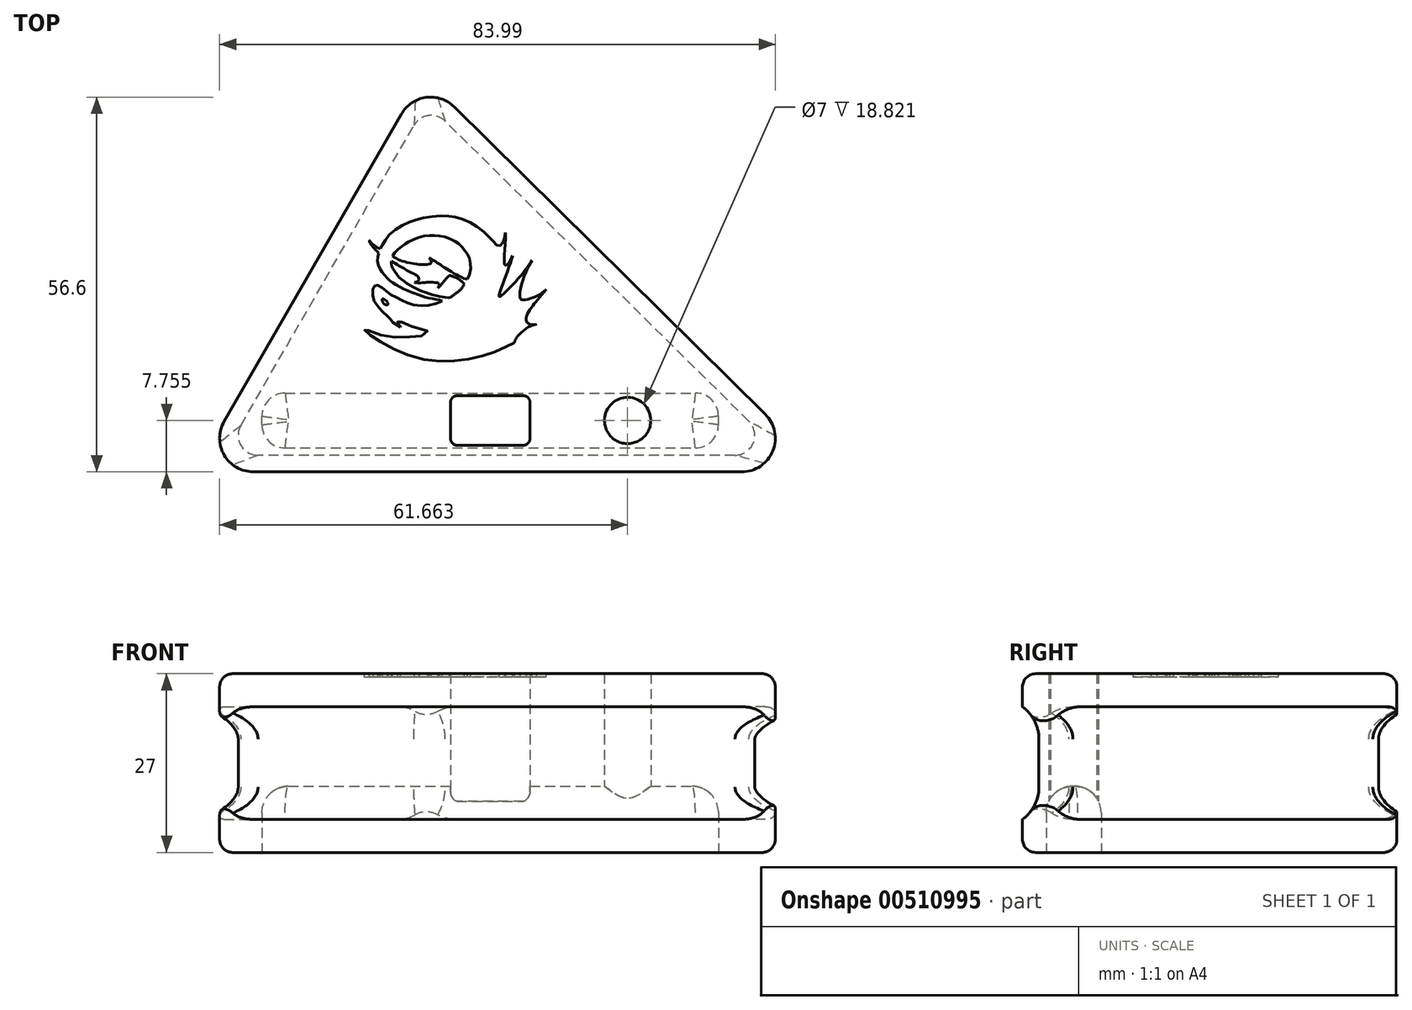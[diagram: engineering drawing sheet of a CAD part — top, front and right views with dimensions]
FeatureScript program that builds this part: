
annotation { "Feature Type Name" : "Feature", "Feature Type Description" : "" }
export const myFeature = defineFeature(function(context is Context, id is Id, definition is map)
    precondition{}
    {
        {
            var Q0;
            Q0=qCreatedBy(makeId("Top.planeOp"),FACE);
            var sketch = newSketch(context, id + "F0", { "sketchPlane" : qUnion([Q0])});
            skLineSegment(sketch, "E0", {"start": v(-34.5, -20.99) * mm, "end": v(60.5, -20.99) * mm});
            skLineSegment(sketch, "E1", {"start": v(0, 38.77) * mm, "end": v(-34.5, -20.99) * mm});
            skLineSegment(sketch, "E2", {"start": v(0, 38.77) * mm, "end": v(60.5, -20.99) * mm});
            skSolve(sketch);
        }
        {
            var Q0;
            Q0=makeQuery(id+"F0.imprint","IMPRINT",FACE,{"disambiguationData":[TD([[makeQuery(id+"F0.imprint","IMPRINT",EDGE,{"derivedFrom":sQuery(id+"F0.wireOp",EDGE,"E0")}),1.0]])]});
            extrude(context, id + "F1", {"entities" : qUnion([Q0]), "depth" : 27 * mm, "offsetDistance" : 25 * mm});
        }
        {
            var Q0;
            Q0=makeQuery(id+"F1.opExtrude","SWEPT_FACE",FACE,{"disambiguationData":[OSD([sQuery(id+"F0.wireOp",EDGE,"E0")])]});
            var sketch = newSketch(context, id + "F2", { "sketchPlane" : qUnion([Q0])});
            skLineSegment(sketch, "E3.bottom", {"start": v(-34.5, 22) * mm, "end": v(60.5, 22) * mm});
            skLineSegment(sketch, "E3.top", {"start": v(-34.5, 5) * mm, "end": v(60.5, 5) * mm});
            skLineSegment(sketch, "E3.left", {"start": v(-34.5, 22) * mm, "end": v(-34.5, 5) * mm});
            skLineSegment(sketch, "E3.right", {"start": v(60.5, 22) * mm, "end": v(60.5, 5) * mm});
            skSolve(sketch);
        }
        {
            var Q0;
            Q0=makeQuery(id+"F2.imprint","IMPRINT",FACE,{"disambiguationData":[TD([[makeQuery(id+"F2.imprint","IMPRINT",EDGE,{"derivedFrom":sQuery(id+"F2.wireOp",EDGE,"E3.bottom")}),-1.0]])]});
            extrude(context, id + "F3", {"entities" : qUnion([Q0]), "operationType" : NewBodyOperationType.REMOVE, "oppositeDirection" : true, "depth" : 2.5 * mm, "offsetDistance" : 25 * mm});
        }
        {
            var Q0;
            Q0=makeQuery(id+"F1.opExtrude","SWEPT_FACE",FACE,{"disambiguationData":[OSD([sQuery(id+"F0.wireOp",EDGE,"E2")])]});
            var sketch = newSketch(context, id + "F4", { "sketchPlane" : qUnion([Q0])});
            skLineSegment(sketch, "E4.bottom", {"start": v(-54.23, 22) * mm, "end": v(27.24, 22) * mm});
            skLineSegment(sketch, "E4.top", {"start": v(-54.23, 5) * mm, "end": v(27.24, 5) * mm});
            skLineSegment(sketch, "E4.left", {"start": v(-54.23, 22) * mm, "end": v(-54.23, 5) * mm});
            skLineSegment(sketch, "E4.right", {"start": v(27.24, 22) * mm, "end": v(27.24, 5) * mm});
            skSolve(sketch);
        }
        {
            var Q0;
            Q0=makeQuery(id+"F4.imprint","IMPRINT",FACE,{"disambiguationData":[TD([[makeQuery(id+"F4.imprint","IMPRINT",EDGE,{"derivedFrom":sQuery(id+"F4.wireOp",EDGE,"E4.bottom")}),-1.0]])]});
            extrude(context, id + "F5", {"entities" : qUnion([Q0]), "operationType" : NewBodyOperationType.REMOVE, "oppositeDirection" : true, "depth" : 2.5 * mm, "offsetDistance" : 25 * mm});
        }
        {
            var Q0;
            Q0=makeQuery(id+"F1.opExtrude","SWEPT_FACE",FACE,{"disambiguationData":[OSD([sQuery(id+"F0.wireOp",EDGE,"E1")])]});
            var sketch = newSketch(context, id + "F6", { "sketchPlane" : qUnion([Q0])});
            skLineSegment(sketch, "E5.bottom", {"start": v(-30.99, 22) * mm, "end": v(32.54, 22) * mm});
            skLineSegment(sketch, "E5.top", {"start": v(-30.99, 5) * mm, "end": v(32.54, 5) * mm});
            skLineSegment(sketch, "E5.left", {"start": v(-30.99, 22) * mm, "end": v(-30.99, 5) * mm});
            skLineSegment(sketch, "E5.right", {"start": v(32.54, 22) * mm, "end": v(32.54, 5) * mm});
            skSolve(sketch);
        }
        {
            var Q0;
            Q0=makeQuery(id+"F6.imprint","IMPRINT",FACE,{"disambiguationData":[TD([[makeQuery(id+"F6.imprint","IMPRINT",EDGE,{"derivedFrom":sQuery(id+"F6.wireOp",EDGE,"E5.bottom")}),-1.0]])]});
            extrude(context, id + "F7", {"entities" : qUnion([Q0]), "operationType" : NewBodyOperationType.REMOVE, "oppositeDirection" : true, "depth" : 2.5 * mm, "offsetDistance" : 25 * mm});
        }
        {
            var Q0;
            Q0=makeQuery(id+"F7.boolean.opBoolean","COPY",EDGE,{"derivedFrom":makeQuery(id+"F7.opExtrude","CAP_EDGE",EDGE,{"disambiguationData":[OSD([sQuery(id+"F6.wireOp",EDGE,"E5.bottom")])],"isStart":false})});
            var Q1;
            Q1=makeQuery(id+"F7.boolean.opBoolean","COPY",EDGE,{"derivedFrom":makeQuery(id+"F7.opExtrude","CAP_EDGE",EDGE,{"disambiguationData":[OSD([sQuery(id+"F6.wireOp",EDGE,"E5.top")])],"isStart":false})});
            var Q2;
            Q2=makeQuery(id+"F3.boolean.opBoolean","COPY",EDGE,{"derivedFrom":makeQuery(id+"F3.opExtrude","CAP_EDGE",EDGE,{"disambiguationData":[OSD([sQuery(id+"F2.wireOp",EDGE,"E3.bottom")])],"isStart":false})});
            var Q3;
            Q3=makeQuery(id+"F3.boolean.opBoolean","COPY",EDGE,{"derivedFrom":makeQuery(id+"F3.opExtrude","CAP_EDGE",EDGE,{"disambiguationData":[OSD([sQuery(id+"F2.wireOp",EDGE,"E3.top")])],"isStart":false})});
            var Q4;
            Q4=makeQuery(id+"F5.boolean.opBoolean","COPY",EDGE,{"derivedFrom":makeQuery(id+"F5.opExtrude","CAP_EDGE",EDGE,{"disambiguationData":[OSD([sQuery(id+"F4.wireOp",EDGE,"E4.bottom")])],"isStart":false})});
            var Q5;
            Q5=makeQuery(id+"F5.boolean.opBoolean","COPY",EDGE,{"derivedFrom":makeQuery(id+"F5.opExtrude","CAP_EDGE",EDGE,{"disambiguationData":[OSD([sQuery(id+"F4.wireOp",EDGE,"E4.top")])],"isStart":false})});
            fillet(context, id + "F8", {"entities" : qUnion([Q0, Q1, Q2, Q3, Q4, Q5]), "radius" : 6 * mm, "tangentPropagation" : true, "allowEdgeOverflow" : false});
        }
        {
            var Q0;
            Q0=makeQuery(id+"F8.opFillet","BLEND_EDGE",EDGE,{"blendedFrom":[makeQuery(id+"F5.boolean.opBoolean","COPY",EDGE,{"derivedFrom":makeQuery(id+"F5.opExtrude","CAP_EDGE",EDGE,{"disambiguationData":[OSD([sQuery(id+"F4.wireOp",EDGE,"E4.bottom")])],"isStart":false})}),makeQuery(id+"F3.boolean.opBoolean","COPY",EDGE,{"derivedFrom":makeQuery(id+"F3.opExtrude","CAP_EDGE",EDGE,{"disambiguationData":[OSD([sQuery(id+"F2.wireOp",EDGE,"E3.bottom")])],"isStart":false})})],"blendedInto":[]});
            var Q1;
            Q1=makeQuery(id+"F8.opFillet","BLEND_EDGE",EDGE,{"blendedFrom":[makeQuery(id+"F7.boolean.opBoolean","COPY",EDGE,{"derivedFrom":makeQuery(id+"F7.opExtrude","CAP_EDGE",EDGE,{"disambiguationData":[OSD([sQuery(id+"F6.wireOp",EDGE,"E5.bottom")])],"isStart":false})}),makeQuery(id+"F5.boolean.opBoolean","COPY",EDGE,{"derivedFrom":makeQuery(id+"F5.opExtrude","CAP_EDGE",EDGE,{"disambiguationData":[OSD([sQuery(id+"F4.wireOp",EDGE,"E4.bottom")])],"isStart":false})})],"blendedInto":[]});
            var Q2;
            Q2=makeQuery(id+"F8.opFillet","BLEND_EDGE",EDGE,{"blendedFrom":[makeQuery(id+"F7.boolean.opBoolean","COPY",EDGE,{"derivedFrom":makeQuery(id+"F7.opExtrude","CAP_EDGE",EDGE,{"disambiguationData":[OSD([sQuery(id+"F6.wireOp",EDGE,"E5.bottom")])],"isStart":false})}),makeQuery(id+"F3.boolean.opBoolean","COPY",EDGE,{"derivedFrom":makeQuery(id+"F3.opExtrude","CAP_EDGE",EDGE,{"disambiguationData":[OSD([sQuery(id+"F2.wireOp",EDGE,"E3.bottom")])],"isStart":false})})],"blendedInto":[]});
            fillet(context, id + "F9", {"entities" : qUnion([Q0, Q1, Q2]), "radius" : 3 * mm, "tangentPropagation" : true, "allowEdgeOverflow" : false});
        }
        {
            var Q0;
            Q0=makeQuery(id+"F1.opExtrude","SWEPT_EDGE",EDGE,{"disambiguationData":[OSD([sQuery(id+"F0.wireOp",EDGE,"F2jWqIrs-Qg5U-4JRb-IFzo-0ohS2Rwvlgda"),sQuery(id+"F0.wireOp",EDGE,"E1")])]});
            var Q1;
            Q1=makeQuery(id+"F1.opExtrude","SWEPT_EDGE",EDGE,{"disambiguationData":[OSD([sQuery(id+"F0.wireOp",EDGE,"E0"),sQuery(id+"F0.wireOp",EDGE,"F2jWqIrs-Qg5U-4JRb-IFzo-0ohS2Rwvlgda")])]});
            var Q2;
            Q2=makeQuery(id+"F1.opExtrude","SWEPT_EDGE",EDGE,{"disambiguationData":[OSD([sQuery(id+"F0.wireOp",EDGE,"E0"),sQuery(id+"F0.wireOp",EDGE,"E1")])]});
            fillet(context, id + "F10", {"entities" : qUnion([Q0, Q1, Q2]), "radius" : 5.08 * mm, "tangentPropagation" : true, "allowEdgeOverflow" : false});
        }
        {
            var Q0;
            Q0=makeQuery(id+"F1.opExtrude","CAP_EDGE",EDGE,{"disambiguationData":[OSD([sQuery(id+"F0.wireOp",EDGE,"E1")])],"isStart":false});
            var Q1;
            Q1=makeQuery(id+"F1.opExtrude","CAP_EDGE",EDGE,{"disambiguationData":[OSD([sQuery(id+"F0.wireOp",EDGE,"E1")])],"isStart":true});
            fillet(context, id + "F11", {"entities" : qUnion([Q0, Q1]), "radius" : 2 * mm, "tangentPropagation" : true, "allowEdgeOverflow" : false});
        }
        {
            var Q0;
            Q0=makeQuery(id+"F0.imprint","IMPRINT",FACE,{"disambiguationData":[TD([[makeQuery(id+"F0.imprint","IMPRINT",EDGE,{"derivedFrom":sQuery(id+"F0.wireOp",EDGE,"E0")}),1.0]])]});
            var sketch = newSketch(context, id + "F12", { "sketchPlane" : qUnion([Q0])});
            skLineSegment(sketch, "E6.bottom", {"start": v(-24.38, -17.39) * mm, "end": v(44.62, -17.39) * mm});
            skLineSegment(sketch, "E6.top", {"start": v(-24.38, -9.09) * mm, "end": v(44.62, -9.09) * mm});
            skLineSegment(sketch, "E6.left", {"start": v(-24.38, -17.39) * mm, "end": v(-24.38, -9.09) * mm});
            skLineSegment(sketch, "E6.right", {"start": v(44.62, -17.39) * mm, "end": v(44.62, -9.09) * mm});
            skSolve(sketch);
        }
        {
            var Q0;
            Q0=makeQuery(id+"F12.imprint","IMPRINT",FACE,{"disambiguationData":[TD([[makeQuery(id+"F12.imprint","IMPRINT",EDGE,{"derivedFrom":sQuery(id+"F12.wireOp",EDGE,"E6.bottom")}),1.0]])]});
            var Q1;
            Q1 = qConstructionFilter(qBodyType(qCreatedBy(id + "F12" ,EDGE), BodyType.WIRE), ConstructionObject.NO);
            extrude(context, id + "F13", {"entities" : qUnion([Q0]), "operationType" : NewBodyOperationType.REMOVE, "surfaceEntities" : qUnion([Q1]), "depth" : 10 * mm, "offsetDistance" : 25 * mm});
        }
        {
            var Q0;
            Q0=makeQuery(id+"F13.boolean.opBoolean","COPY",EDGE,{"derivedFrom":makeQuery(id+"F13.opExtrude","SWEPT_EDGE",EDGE,{"disambiguationData":[OSD([sQuery(id+"F12.wireOp",EDGE,"E6.bottom"),sQuery(id+"F12.wireOp",EDGE,"E6.left")])]})});
            var Q1;
            Q1=makeQuery(id+"F13.boolean.opBoolean","COPY",EDGE,{"derivedFrom":makeQuery(id+"F13.opExtrude","SWEPT_EDGE",EDGE,{"disambiguationData":[OSD([sQuery(id+"F12.wireOp",EDGE,"E6.top"),sQuery(id+"F12.wireOp",EDGE,"E6.left")])]})});
            var Q2;
            Q2=makeQuery(id+"F13.boolean.opBoolean","COPY",EDGE,{"derivedFrom":makeQuery(id+"F13.opExtrude","SWEPT_EDGE",EDGE,{"disambiguationData":[OSD([sQuery(id+"F12.wireOp",EDGE,"E6.bottom"),sQuery(id+"F12.wireOp",EDGE,"E6.right")])]})});
            var Q3;
            Q3=makeQuery(id+"F13.boolean.opBoolean","COPY",EDGE,{"derivedFrom":makeQuery(id+"F13.opExtrude","SWEPT_EDGE",EDGE,{"disambiguationData":[OSD([sQuery(id+"F12.wireOp",EDGE,"E6.top"),sQuery(id+"F12.wireOp",EDGE,"E6.right")])]})});
            fillet(context, id + "F14", {"entities" : qUnion([Q0, Q1, Q2, Q3]), "radius" : 3.5 * mm, "tangentPropagation" : true, "allowEdgeOverflow" : false});
        }
        {
            var Q0;
            Q0=makeQuery(id+"F13.boolean.opBoolean","COPY",EDGE,{"derivedFrom":makeQuery(id+"F13.opExtrude","CAP_EDGE",EDGE,{"disambiguationData":[OSD([sQuery(id+"F12.wireOp",EDGE,"E6.top")])],"isStart":false})});
            var Q1;
            Q1=makeQuery(id+"F13.boolean.opBoolean","COPY",EDGE,{"derivedFrom":makeQuery(id+"F13.opExtrude","CAP_EDGE",EDGE,{"disambiguationData":[OSD([sQuery(id+"F12.wireOp",EDGE,"E6.bottom")])],"isStart":false})});
            fillet(context, id + "F15", {"entities" : qUnion([Q0, Q1]), "radius" : 4 * mm, "tangentPropagation" : true, "allowEdgeOverflow" : false});
        }
        {
            var Q0;
            Q0=makeQuery(id+"F13.boolean.opBoolean","COPY",FACE,{"derivedFrom":makeQuery(id+"F13.opExtrude","CAP_FACE",FACE,{"disambiguationData":[OSD([sQuery(id+"F12.wireOp",EDGE,"E6.bottom"),sQuery(id+"F12.wireOp",EDGE,"E6.top"),sQuery(id+"F12.wireOp",EDGE,"E6.left"),sQuery(id+"F12.wireOp",EDGE,"E6.right")])],"isStart":false})});
            var sketch = newSketch(context, id + "F16", { "sketchPlane" : qUnion([Q0])});
            skLineSegment(sketch, "E7.bottom", {"start": v(16.12, 9.48) * mm, "end": v(4.12, 9.48) * mm});
            skLineSegment(sketch, "E7.top", {"start": v(16.12, 16.98) * mm, "end": v(4.12, 16.98) * mm});
            skLineSegment(sketch, "E7.left", {"start": v(16.12, 9.48) * mm, "end": v(16.12, 16.98) * mm});
            skLineSegment(sketch, "E7.right", {"start": v(4.12, 9.48) * mm, "end": v(4.12, 16.98) * mm});
            skPoint(sketch, "E7.middle", {"position": v(10.12, 13.23) * mm});
            skPoint(sketch, "E7.middle.positionSnap0", {"position": v(10.12, 13.39) * mm});
            skPoint(sketch, "E7.centerSnap0", {"position": v(10.12, 13.39) * mm});
            skSolve(sketch);
        }
        {
            var Q0;
            Q0 = qSketchRegion(id + "F16", true);
            extrude(context, id + "F17", {"entities" : qUnion([Q0]), "operationType" : NewBodyOperationType.REMOVE, "oppositeDirection" : true, "depth" : 19.4 * mm, "hasSecondDirection" : true, "secondDirectionOppositeDirection" : false, "secondDirectionDepth" : 22.6 * mm, "offsetDistance" : 25 * mm});
        }
        {
            var Q0;
            Q0=makeQuery(id+"F17.boolean.opBoolean","COPY",EDGE,{"derivedFrom":makeQuery(id+"F17.opExtrude","SWEPT_EDGE",EDGE,{"disambiguationData":[OSD([sQuery(id+"F16.wireOp",EDGE,"E7.bottom"),sQuery(id+"F16.wireOp",EDGE,"E7.left")])]})});
            var Q1;
            Q1=makeQuery(id+"F17.boolean.opBoolean","COPY",EDGE,{"derivedFrom":makeQuery(id+"F17.opExtrude","SWEPT_EDGE",EDGE,{"disambiguationData":[OSD([sQuery(id+"F16.wireOp",EDGE,"E7.bottom"),sQuery(id+"F16.wireOp",EDGE,"E7.right")])]})});
            var Q2;
            Q2=makeQuery(id+"F17.boolean.opBoolean","COPY",EDGE,{"derivedFrom":makeQuery(id+"F17.opExtrude","SWEPT_EDGE",EDGE,{"disambiguationData":[OSD([sQuery(id+"F16.wireOp",EDGE,"E7.top"),sQuery(id+"F16.wireOp",EDGE,"E7.left")])]})});
            var Q3;
            Q3=makeQuery(id+"F17.boolean.opBoolean","COPY",EDGE,{"derivedFrom":makeQuery(id+"F17.opExtrude","SWEPT_EDGE",EDGE,{"disambiguationData":[OSD([sQuery(id+"F16.wireOp",EDGE,"E7.top"),sQuery(id+"F16.wireOp",EDGE,"E7.right")])]})});
            fillet(context, id + "F18", {"entities" : qUnion([Q0, Q1, Q2, Q3]), "radius" : 1 * mm, "tangentPropagation" : true, "allowEdgeOverflow" : false});
        }
        {
            var Q0;
            Q0=makeQuery(id+"F1.opExtrude","CAP_FACE",FACE,{"disambiguationData":[OSD([sQuery(id+"F0.wireOp",EDGE,"E0"),sQuery(id+"F0.wireOp",EDGE,"E1"),sQuery(id+"F0.wireOp",EDGE,"E2")])],"isStart":false});
            var sketch = newSketch(context, id + "F19", { "sketchPlane" : qUnion([Q0])});
            skFitSpline(sketch, "E8", {"points": [v(2.88, 4.8) * mm, v(1.9, 5.06) * mm, v(0.82, 5.28) * mm, v(-0.36, 5.6) * mm, v(-1.5, 6.03) * mm, v(-3.03, 6.69) * mm, v(-4.46, 7.45) * mm, v(-5.45, 8.26) * mm, v(-6.3, 9.3) * mm, v(-6.88, 10.61) * mm, v(-6.74, 12.05) * mm], "startDerivative": vector(-7.56, 5.16) * mm, "endDerivative": vector(3.22, 10.93) * mm});
            skFitSpline(sketch, "E9", {"points": [v(-6.74, 12.05) * mm, v(-7.2, 12.52) * mm, v(-7.71, 13.12) * mm, v(-8.03, 13.59) * mm, v(-8.16, 13.86) * mm, v(-8.16, 13.93) * mm, v(-7.68, 13.43) * mm, v(-7.17, 13.05) * mm, v(-6.51, 12.73) * mm], "startDerivative": vector(-3.25, 3.3) * mm, "endDerivative": vector(4.22, -0.84) * mm});
            skFitSpline(sketch, "E10", {"points": [v(-6.51, 12.73) * mm, v(-6.35, 12.98) * mm, v(-6.1, 13.43) * mm, v(-5.72, 14.02) * mm, v(-5.16, 14.8) * mm, v(-4.05, 15.7) * mm, v(-2.97, 16.36) * mm, v(-1.85, 16.82) * mm, v(-0.95, 17.12) * mm, v(0.5, 17.43) * mm, v(2.02, 17.64) * mm, v(3.63, 17.64) * mm, v(4.63, 17.52) * mm, v(5.4, 17.32) * mm, v(7, 16.72) * mm, v(8.02, 16.08) * mm, v(9.26, 15.2) * mm, v(10.06, 14.34) * mm, v(10.58, 13.81) * mm, v(11, 13.34) * mm, v(11.25, 13.17) * mm, v(11.49, 13.16) * mm, v(11.78, 13.29) * mm, v(12.02, 13.63) * mm, v(12.24, 14.18) * mm, v(12.36, 14.75) * mm, v(12.4, 15.15) * mm], "startDerivative": vector(6.55, 10.15) * mm, "endDerivative": vector(1.37, 14.38) * mm});
            skFitSpline(sketch, "E11", {"points": [v(12.4, 15.15) * mm, v(12.47, 14.53) * mm, v(12.41, 13.6) * mm, v(12.28, 12.37) * mm, v(12.23, 11.38) * mm, v(12.24, 10.84) * mm, v(12.28, 10.37) * mm, v(12.35, 10.26) * mm, v(12.48, 10.22) * mm, v(12.72, 10.33) * mm, v(13, 10.7) * mm, v(13.5, 11.68) * mm], "startDerivative": vector(1, -6.2) * mm, "endDerivative": vector(3.78, 8.75) * mm});
            skFitSpline(sketch, "E12", {"points": [v(13.5, 11.68) * mm, v(13.25, 10.74) * mm, v(12.86, 9.7) * mm, v(12.4, 8.4) * mm, v(11.98, 7.28) * mm, v(11.63, 6.23) * mm, v(11.46, 5.73) * mm, v(11.43, 5.5) * mm, v(11.46, 5.46) * mm, v(11.6, 5.46) * mm, v(11.9, 5.73) * mm, v(12.4, 6.14) * mm, v(12.95, 6.7) * mm, v(14.02, 7.81) * mm, v(14.96, 8.92) * mm, v(16.47, 10.98) * mm], "startDerivative": vector(-3.06, -14.57) * mm, "endDerivative": vector(13.16, 19.12) * mm});
            skFitSpline(sketch, "E13", {"points": [v(16.47, 10.98) * mm, v(15.36, 8.76) * mm, v(14.76, 6.96) * mm, v(14.58, 5.72) * mm, v(14.62, 5.31) * mm, v(14.79, 5.06) * mm, v(15.1, 4.97) * mm, v(15.62, 5.03) * mm, v(16.4, 5.26) * mm, v(17.19, 5.58) * mm, v(17.97, 6.1) * mm, v(18.58, 6.57) * mm], "startDerivative": vector(-12.66, -21.05) * mm, "endDerivative": vector(6.32, 5.86) * mm});
            skFitSpline(sketch, "E14", {"points": [v(18.58, 6.57) * mm, v(17.02, 4.7) * mm, v(16.3, 3.77) * mm, v(15.64, 2.56) * mm, v(15.57, 1.81) * mm, v(15.78, 1.5) * mm, v(16.09, 1.3) * mm, v(16.61, 1.24) * mm, v(17.13, 1.29) * mm], "startDerivative": vector(-8.12, -9.68) * mm, "endDerivative": vector(5.18, 0.73) * mm});
            skFitSpline(sketch, "E15", {"points": [v(17.13, 1.29) * mm, v(16.1, 0.98) * mm, v(15.32, 0.46) * mm, v(14.71, -0.02) * mm, v(14.36, -0.38) * mm, v(14.02, -0.86) * mm, v(13.8, -1.27) * mm, v(13.77, -1.51) * mm], "startDerivative": vector(-5.77, -1.3) * mm, "endDerivative": vector(-0.14, -2.56) * mm});
            skFitSpline(sketch, "E16", {"points": [v(13.77, -1.51) * mm, v(13.35, -1.69) * mm, v(12.73, -2) * mm, v(12.03, -2.33) * mm, v(10.66, -2.9) * mm, v(9.56, -3.3) * mm, v(8.47, -3.6) * mm, v(6.78, -3.97) * mm, v(5.28, -4.2) * mm, v(3.7, -4.28) * mm, v(2.14, -4.28) * mm, v(0.12, -4.06) * mm, v(-1.93, -3.47) * mm, v(-3.58, -2.81) * mm, v(-5.17, -2.1) * mm, v(-6.55, -1.31) * mm, v(-7.57, -0.63) * mm, v(-8.23, -0.14) * mm, v(-8.56, 0.16) * mm, v(-8.8, 0.38) * mm, v(-8.92, 0.47) * mm, v(-8.92, 0.55) * mm, v(-8.79, 0.6) * mm, v(-8.46, 0.46) * mm, v(-7.53, 0.03) * mm, v(-5.96, -0.47) * mm, v(-4.53, -0.66) * mm, v(-3.13, -0.66) * mm, v(-1.37, -0.57) * mm, v(-0.51, -0.48) * mm, v(0.06, -0.4) * mm, v(0.3, -0.2) * mm, v(0.6, 0.28) * mm, v(0.61, 0.34) * mm, v(0.57, 0.41) * mm, v(0.21, 0.47) * mm, v(-0.46, 0.6) * mm, v(-1.2, 0.77) * mm, v(-2.09, 1.11) * mm, v(-2.9, 1.46) * mm, v(-3.43, 1.7) * mm, v(-3.73, 1.83) * mm, v(-3.87, 1.81) * mm, v(-3.95, 1.69) * mm, v(-3.8, 1.4) * mm, v(-3.52, 1.08) * mm, v(-3.47, 0.97) * mm, v(-3.45, 0.88) * mm], "startDerivative": vector(-23.7, -9.36) * mm, "endDerivative": vector(2.17, -11.37) * mm});
            skFitSpline(sketch, "E17", {"points": [v(-3.45, 0.88) * mm, v(-3.68, 1) * mm, v(-4.26, 1.38) * mm, v(-4.79, 1.79) * mm, v(-5.15, 2.27) * mm, v(-5.62, 2.71) * mm, v(-6.27, 3.35) * mm, v(-6.77, 3.92) * mm, v(-7.08, 4.3) * mm, v(-7.38, 4.72) * mm, v(-7.6, 5.68) * mm, v(-7.59, 6.65) * mm, v(-7.41, 7) * mm, v(-7.17, 7.2) * mm, v(-6.87, 7.18) * mm, v(-6.23, 6.8) * mm, v(-5.56, 6.28) * mm, v(-4.74, 5.67) * mm, v(-3.8, 5.21) * mm, v(-2.79, 4.7) * mm, v(-1.65, 4.3) * mm, v(0, 4.1) * mm, v(1.47, 4.3) * mm, v(2.88, 4.8) * mm], "startDerivative": vector(-8.16, 4.17) * mm, "endDerivative": vector(15.97, 12.28) * mm});
            skFitSpline(sketch, "E18", {"points": [v(6.2, 7.3) * mm, v(5.96, 7.62) * mm, v(5.5, 8.01) * mm, v(4.98, 8.32) * mm, v(4.4, 8.54) * mm, v(3.95, 8.68) * mm], "startDerivative": vector(-1.19, 1.81) * mm, "endDerivative": vector(-3.1, 0.78) * mm});
            skFitSpline(sketch, "E19", {"points": [v(3.95, 8.68) * mm, v(3.57, 8.3) * mm, v(3.15, 7.8) * mm, v(2.55, 7.1) * mm, v(2.2, 6.78) * mm], "startDerivative": vector(-1.7, -1.58) * mm, "endDerivative": vector(-1.5, -1.28) * mm});
            skFitSpline(sketch, "E20", {"points": [v(2.2, 6.78) * mm, v(2.4, 7.14) * mm, v(2.3, 7.5) * mm, v(1.93, 7.6) * mm, v(0.92, 7.65) * mm, v(0.07, 7.58) * mm, v(-0.97, 7.57) * mm, v(-1.36, 7.63) * mm], "startDerivative": vector(2.36, 2.84) * mm, "endDerivative": vector(-2.86, 0.53) * mm});
            skFitSpline(sketch, "E21", {"points": [v(-1.36, 7.63) * mm, v(-0.82, 7.79) * mm, v(-0.64, 8.11) * mm, v(-0.88, 8.59) * mm, v(-1.76, 9.08) * mm, v(-2.71, 9.6) * mm, v(-3.57, 10.1) * mm, v(-4.84, 10.83) * mm], "startDerivative": vector(5.12, 0.87) * mm, "endDerivative": vector(-7.01, 3.97) * mm});
            skFitSpline(sketch, "E22", {"points": [v(-4.84, 10.83) * mm, v(-4.82, 10.28) * mm, v(-4.58, 9.68) * mm, v(-3.97, 8.78) * mm, v(-3.16, 7.97) * mm, v(-2.34, 7.41) * mm, v(-1.45, 6.88) * mm, v(-0.36, 6.37) * mm, v(0.53, 6.07) * mm, v(1.9, 5.63) * mm, v(2.82, 5.43) * mm, v(3.56, 5.34) * mm, v(4.12, 5.35) * mm], "startDerivative": vector(-0.27, -8.5) * mm, "endDerivative": vector(4.83, 0.85) * mm});
            skFitSpline(sketch, "E23", {"points": [v(4.12, 5.35) * mm, v(4.75, 5.85) * mm, v(5.57, 6.46) * mm, v(6.2, 7.3) * mm], "startDerivative": vector(1.94, 1.63) * mm, "endDerivative": vector(1.61, 2.58) * mm});
            skFitSpline(sketch, "E24", {"points": [v(6.66, 8.12) * mm, v(5.96, 8.29) * mm, v(5.23, 8.67) * mm, v(4.46, 9.1) * mm, v(4.42, 9.13) * mm, v(3.64, 9.59) * mm, v(2.8, 10.14) * mm, v(2.19, 10.54) * mm, v(1.6, 10.94) * mm, v(0.9, 11.33) * mm], "startDerivative": vector(-6.32, 1.22) * mm, "endDerivative": vector(-6.08, 3.1) * mm});
            skFitSpline(sketch, "E25", {"points": [v(0.9, 11.33) * mm, v(1.19, 10.91) * mm, v(1.15, 10.51) * mm, v(0.43, 10.33) * mm, v(-0.58, 10.34) * mm, v(-2.13, 10.56) * mm, v(-3.54, 11) * mm, v(-4.66, 11.58) * mm], "startDerivative": vector(3.35, -3.72) * mm, "endDerivative": vector(-6.56, 3.7) * mm});
            skFitSpline(sketch, "E26", {"points": [v(-4.66, 11.58) * mm, v(-4.19, 12.28) * mm, v(-3.39, 12.97) * mm, v(-2.65, 13.51) * mm, v(-1.89, 13.93) * mm, v(-0.55, 14.45) * mm, v(0.95, 14.72) * mm, v(2.04, 14.7) * mm, v(3.39, 14.46) * mm, v(4.78, 13.84) * mm, v(5.49, 13.34) * mm, v(6.15, 12.59) * mm, v(6.74, 11.79) * mm, v(7.05, 10.86) * mm, v(7.12, 9.42) * mm, v(6.66, 8.12) * mm], "startDerivative": vector(7.26, 12.35) * mm, "endDerivative": vector(-6.97, -11.14) * mm});
            skFitSpline(sketch, "E27", {"points": [v(-6.19, 5.17) * mm, v(-6.2, 4.89) * mm, v(-6.07, 4.56) * mm, v(-5.83, 4.3) * mm, v(-5.7, 4.26) * mm, v(-5.38, 4.25) * mm], "startDerivative": vector(-0.21, -1.4) * mm, "endDerivative": vector(1.69, 0.43) * mm});
            skFitSpline(sketch, "E28", {"points": [v(-5.38, 4.25) * mm, v(-5.35, 4.44) * mm, v(-5.47, 4.74) * mm, v(-5.67, 4.91) * mm, v(-5.9, 5.06) * mm, v(-6.19, 5.17) * mm], "startDerivative": vector(0.3, 1.06) * mm, "endDerivative": vector(-1.48, 0.41) * mm});
            skSolve(sketch);
        }
        {
            var Q0;
            Q0=makeQuery(id+"F19.imprint","IMPRINT",FACE,{"disambiguationData":[TD([[makeQuery(id+"F19.imprint","IMPRINT",EDGE,{"derivedFrom":sQuery(id+"F19.wireOp",EDGE,"E8")}),-1.0]])]});
            extrude(context, id + "F20", {"entities" : qUnion([Q0]), "operationType" : NewBodyOperationType.REMOVE, "oppositeDirection" : true, "depth" : 0.5 * mm});
        }
        {
            var Q0;
            Q0=makeQuery(id+"F1.opExtrude","CAP_FACE",FACE,{"disambiguationData":[OSD([sQuery(id+"F0.wireOp",EDGE,"E0"),sQuery(id+"F0.wireOp",EDGE,"E1"),sQuery(id+"F0.wireOp",EDGE,"E2")])],"isStart":true});
            var sketch = newSketch(context, id + "F21", { "sketchPlane" : qUnion([Q0])});
            skCircle(sketch, "E29", {"center": v(30.88, 13.24) * mm, "radius": 3.5 * mm});
            skSolve(sketch);
        }
        {
            var Q0;
            Q0 = qSketchRegion(id + "F21", true);
            var Q1;
            {var subQ1=sQuery(id+"F16.wireOp",EDGE,"E7.bottom");var subQ4=sQuery(id+"F0.wireOp",EDGE,"E2");var subQ5=sQuery(id+"F0.wireOp",EDGE,"E1");var subQ6=sQuery(id+"F0.wireOp",EDGE,"E0");var subQ7=makeQuery(id+"F1.opExtrude","CAP_FACE",FACE,{"disambiguationData":[OSD([subQ6,subQ5,subQ4])],"isStart":false});Q1=makeQuery(id+"F20.boolean.opBoolean","SPLIT",FACE,{"disambiguationData":[TD([makeQuery(id+"F17.boolean.opBoolean","COPY",FACE,{"derivedFrom":makeQuery(id+"F17.opExtrude","SWEPT_FACE",FACE,{"disambiguationData":[OSD([subQ1])]})})])],"derivedFrom":subQ7});}
            extrude(context, id + "F22", {"entities" : qUnion([Q0]), "operationType" : NewBodyOperationType.REMOVE, "endBound" : BoundingType.UP_TO_SURFACE, "oppositeDirection" : true, "depth" : 25.5 * mm, "endBoundEntityFace" : qUnion([Q1]), "offsetDistance" : 25 * mm});
        }
    });
